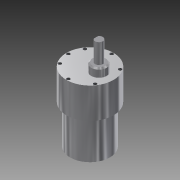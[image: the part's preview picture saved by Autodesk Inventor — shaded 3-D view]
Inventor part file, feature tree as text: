
AUTODESK INVENTOR PART (.ipt)
format: ipt  version: 2014 (Build 180170000, 170)  size: 171,008 bytes
history: native  units: mm
features: sketch x8, thread x8, extrude x6, hole x6, chamfer x1
ambient origin geometry x8: Origin, YZ Plane, XZ Plane, XY Plane, X Axis, Y Axis, Z Axis, Center Point
bodies: Solid1 (feature_tree)
feature tree (29):
  extrude  "Extrusion1"  Depth=30.0mm TaperAngle=0.0deg
  extrude  "Extrusion2"  Depth=24.0mm TaperAngle=0.0deg
  sketch  "Sketch3"  dims[d6=7.0mm d7=6.0mm]
  extrude  "Extrusion3"  Depth=6.0mm
  extrude  "Extrusion4"  Depth=22.0mm TaperAngle=0.0deg
  chamfer  "Chamfer1"  Distance=6.5mm
  sketch  "Sketch4"  dims[d8=12.0mm d9=22.0mm d10=0.0mm d11=6.5mm d12=0.0mm]
  extrude  "Extrusion5"  Depth=2.4mm
  sketch  "Sketch6"  dims[d17=12.0mm d18=0.0mm d19=4.0mm]
  sketch  "Sketch8"  dims[d20=1.0mm d49=16.95mm d50=2.5mm d51=16.95mm]
  sketch  "Sketch9"  dims[d52=2.5mm d53=2.5mm d54=6.0mm d55=4.0mm d56=2.0mm d57=90.0deg d58=0.5mm d59=20.594885mm d60=10.0mm d61=0.0mm d62=10.0mm d63=0.0mm d64=10.0mm d65=0.0mm d66=16.95mm d67=2.5mm d68=15.5mm d69=2.5mm d71=2.5mm d72=15.5mm d73=2.5mm d74=6.0mm d75=4.0mm d76=2.0mm d77=90.0deg d78=0.5mm d79=20.594885mm d80=2.5mm d81=6.0mm d82=4.0mm d83=2.0mm d84=90.0deg d85=0.5mm d86=20.594885mm d87=10.0mm d88=0.0mm d89=10.0mm d90=0.0mm d105=2.5mm d106=6.0mm d107=4.0mm d108=2.0mm d109=90.0deg d110=0.5mm d111=20.594885mm d112=10.0mm d113=0.0mm d116=2.5mm d117=2.5mm d118=2.5mm d119=6.0mm d120=4.0mm d121=2.0mm d122=90.0deg d123=0.5mm d124=20.594885mm d125=2.5mm d126=6.0mm d127=4.0mm d128=2.0mm d129=90.0deg d130=0.5mm d131=20.594885mm d132=10.0mm d133=0.0mm d134=10.0mm d135=0.0mm d136=10.0mm d137=0.0mm]
  hole  "Hole2"  [1 undecoded]
  extrude  "Extrusion9"  Depth=16.95mm
  thread  "Thread5"  [1 undecoded]
  thread  "Thread6"  [1 undecoded]
  hole  "Hole3"  [1 undecoded]
  hole  "Hole4"  [1 undecoded]
  thread  "Thread7"  [1 undecoded]
  thread  "Thread8"  [1 undecoded]
  hole  "Hole7"  [1 undecoded]
  thread  "Thread9"  [1 undecoded]
  hole  "Hole8"  [1 undecoded]
  hole  "Hole9"  [1 undecoded]
  thread  "Thread10"  [1 undecoded]
  thread  "Thread11"  [1 undecoded]
  thread  "Thread12"  [1 undecoded]
  sketch  "Sketch1"  dims[d0=31.0mm d1=30.0mm d2=0.0mm]
  sketch  "Sketch2"  dims[d3=36.8mm d4=24.0mm d5=0.0mm]
  sketch  "Sketch5"  dims[d13=1.0mm d14=2.0mm d15=45.0deg d16=2.4mm]
note: 14 required parameter values undecoded (feature->parameter linkage not recoverable at this tier; creation-order binding heuristic only, values carry confidence <= 0.55)
